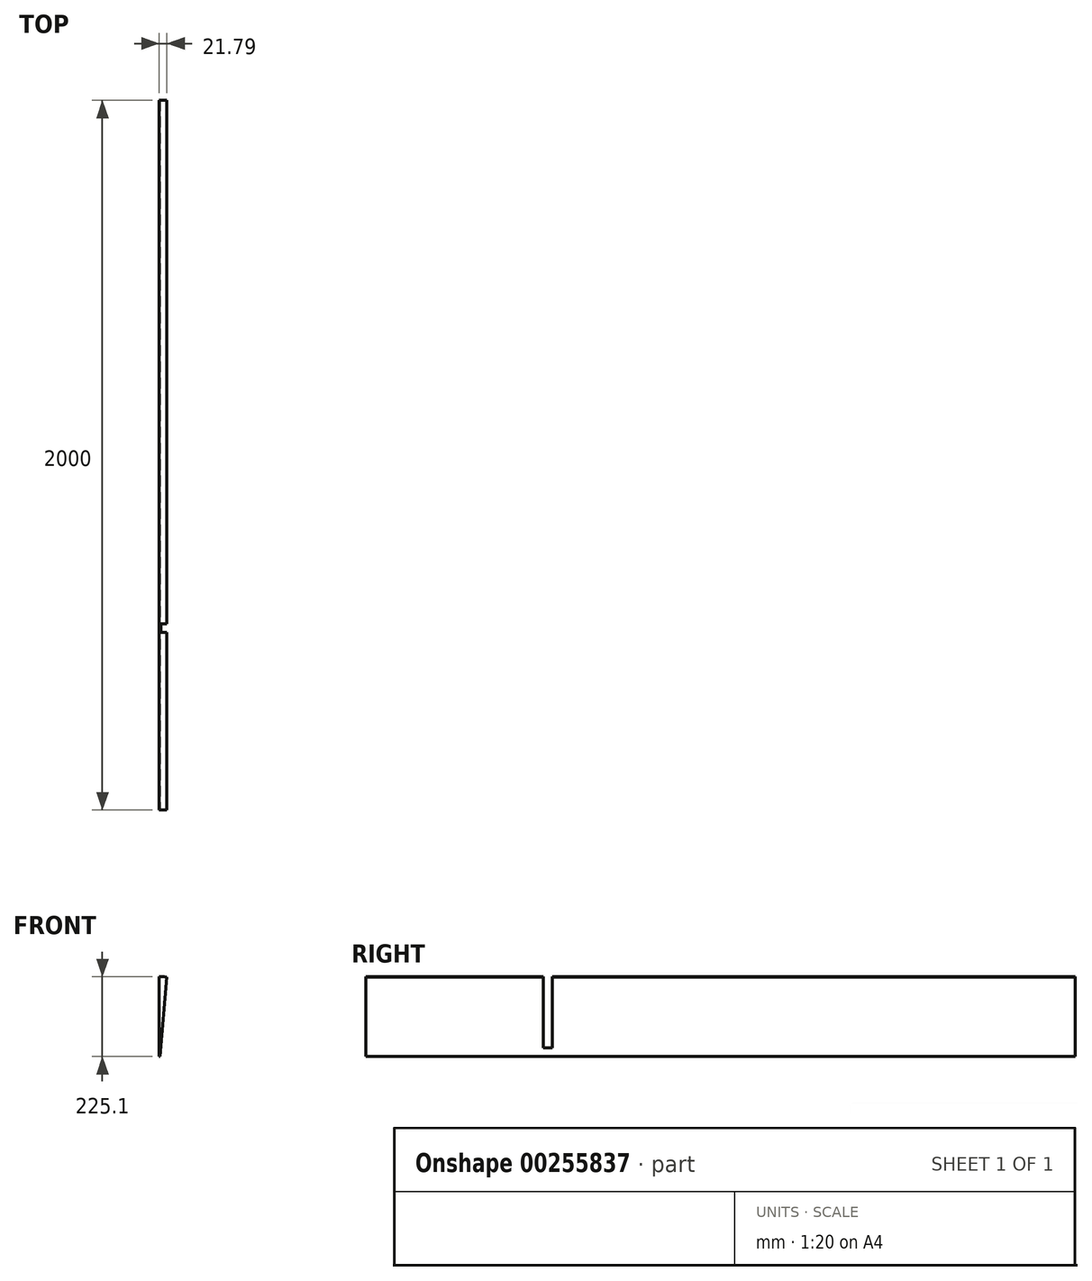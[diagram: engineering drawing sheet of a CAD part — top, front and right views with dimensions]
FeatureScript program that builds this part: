
annotation { "Feature Type Name" : "Feature", "Feature Type Description" : "" }
export const myFeature = defineFeature(function(context is Context, id is Id, definition is map)
    precondition{}
    {
        {
            var Q0;
            Q0=qCreatedBy(makeId("Front.planeOp"),FACE);
            var sketch = newSketch(context, id + "F0", { "sketchPlane" : qUnion([Q0])});
            skCircle(sketch, "E0", {"center": v(0, 0) * mm, "radius": 250 * mm});
            skSolve(sketch);
        }
        {
            var Q0;
            Q0=makeQuery(id+"F0.imprint","IMPRINT",FACE,{"disambiguationData":[TD([[makeQuery(id+"F0.imprint","IMPRINT",EDGE,{"derivedFrom":sQuery(id+"F0.wireOp",EDGE,"E0")}),1.0]])]});
            extrude(context, id + "F1", {"entities" : qUnion([Q0]), "depth" : 2000 * mm});
        }
        {
            var Q0;
            Q0=qCreatedBy(makeId("Front.planeOp"),FACE);
            cPlane(context, id + "F2", {"entities" : qUnion([Q0]), "cplaneType" : CPlaneType.OFFSET, "offset" : 1475 * mm, "width" : 150 * mm, "height" : 150 * mm});
        }
        {
            var Q0;
            Q0=qCreatedBy(id+"F2.planeOp",FACE);
            var sketch = newSketch(context, id + "F3", { "sketchPlane" : qUnion([Q0])});
            skCircle(sketch, "E1", {"center": v(0, 0) * mm, "radius": 250 * mm});
            skCircle(sketch, "E2", {"center": v(0, 0) * mm, "radius": 50 * mm});
            skSolve(sketch);
        }
        {
            var Q0;
            Q0=makeQuery(id+"F3.imprint","IMPRINT",FACE,{"disambiguationData":[TD([[makeQuery(id+"F3.imprint","IMPRINT",EDGE,{"derivedFrom":sQuery(id+"F3.wireOp",EDGE,"E1")}),1.0]])]});
            extrude(context, id + "F4", {"entities" : qUnion([Q0]), "operationType" : NewBodyOperationType.REMOVE, "depth" : 25 * mm});
        }
        {
            var Q0;
            Q0=makeQuery(id+"F1.opExtrude","CAP_FACE",FACE,{"disambiguationData":[OSD([sQuery(id+"F0.wireOp",EDGE,"E0")])],"isStart":false});
            var sketch = newSketch(context, id + "F5", { "sketchPlane" : qUnion([Q0])});
            skLineSegment(sketch, "E3", {"start": v(0, 289.53) * mm, "end": v(0, 0) * mm});
            skLineSegment(sketch, "E4", {"start": v(0, 0) * mm, "end": v(32.85, 375.42) * mm});
            skLineSegment(sketch, "E5", {"start": v(32.85, 375.42) * mm, "end": v(0, 289.53) * mm});
            skCircle(sketch, "E6", {"center": v(0, 0) * mm, "radius": 25 * mm});
            skSolve(sketch);
        }
        {
            var Q0;
            {var subQ0=sQuery(id+"F5.wireOp",EDGE,"E6");var subQ1=sQuery(id+"F5.wireOp",EDGE,"E3");var subQ2=makeQuery(id+"F5.imprint","INTERSECT",VERTEX,{"derivedFrom":[subQ1,subQ0]});Q0=makeQuery(id+"F5.imprint","IMPRINT",FACE,{"disambiguationData":[TD([[makeQuery(id+"F5.imprint","IMPRINT",EDGE,{"disambiguationData":[TD([[subQ2,1.0]])],"derivedFrom":subQ1}),1.0]])]});}
            extrude(context, id + "F6", {"entities" : qUnion([Q0]), "operationType" : NewBodyOperationType.INTERSECT, "oppositeDirection" : true, "depth" : 2000 * mm});
        }
    });
